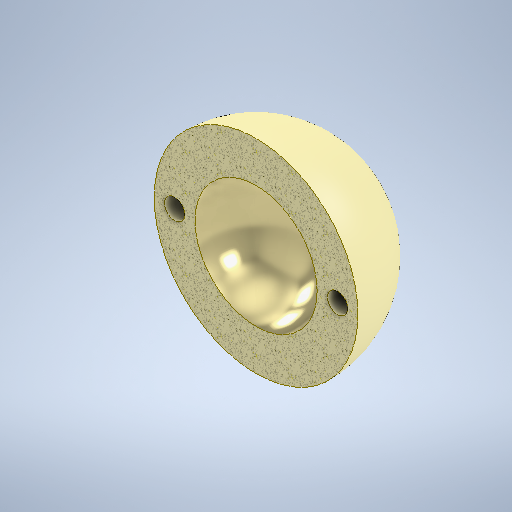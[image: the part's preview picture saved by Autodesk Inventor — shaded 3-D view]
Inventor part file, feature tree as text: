
AUTODESK INVENTOR PART (.ipt)
format: ipt  version: 2025.2 (Build 292293000, 293)  size: 345,600 bytes
history: native  units: mm
features: other x3, sketch x2
ambient origin geometry x8: Origin, YZ Plane, XZ Plane, XY Plane, X Axis, Y Axis, Z Axis, Center Point
bodies: Body1 (feature_tree)
feature tree (5):
  other  "Sólido1"
  other  "Revolução1"
  other  "Revolução2"
  sketch  "Esboço1"  dims[d0=10.0mm]
  sketch  "Esboço2"  dims[d2=3.0mm d3=360.0deg d4=1.0mm d5=4.0mm d6=10.0mm d7=360.0deg]
